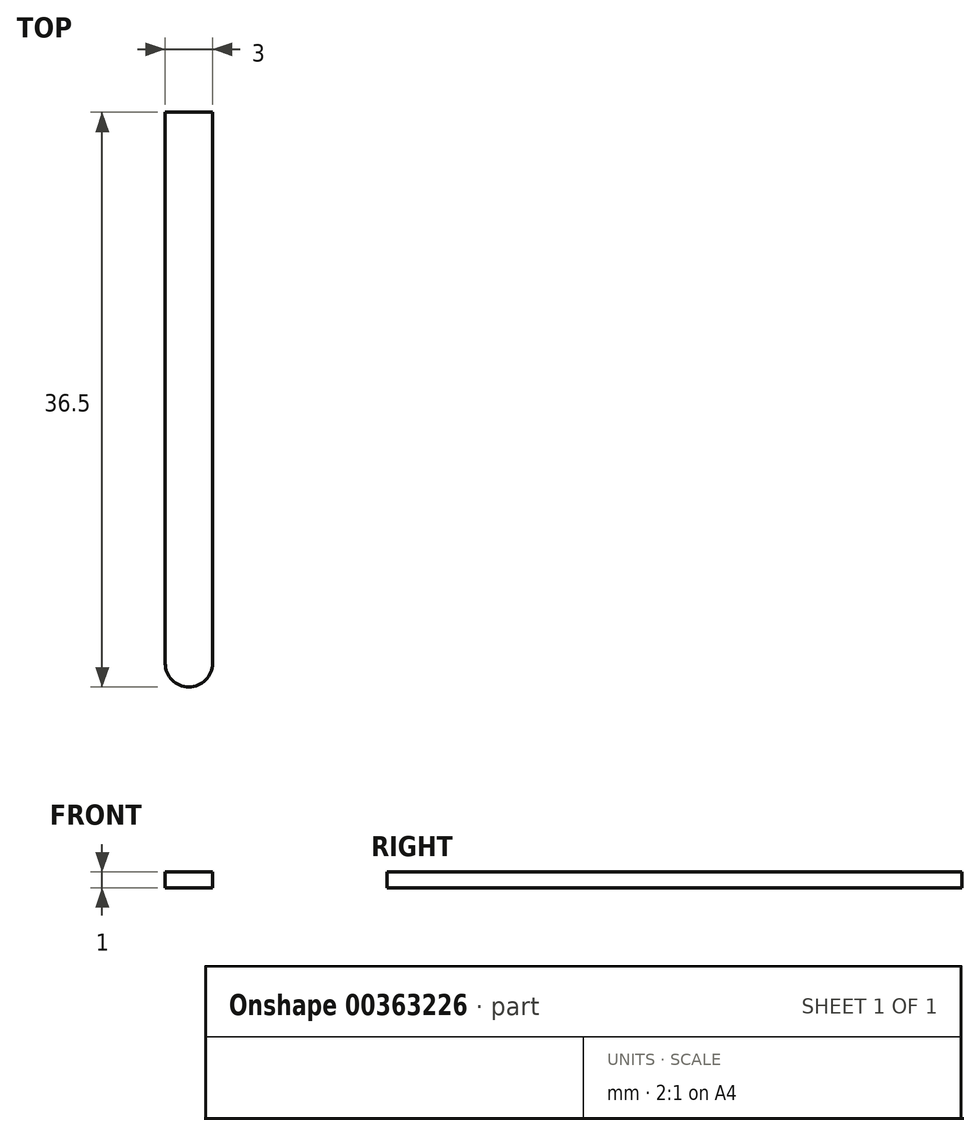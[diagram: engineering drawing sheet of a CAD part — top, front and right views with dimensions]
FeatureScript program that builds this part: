
annotation { "Feature Type Name" : "Feature", "Feature Type Description" : "" }
export const myFeature = defineFeature(function(context is Context, id is Id, definition is map)
    precondition{}
    {
        {
            var Q0;
            Q0=qCreatedBy(makeId("Top.planeOp"),FACE);
            var sketch = newSketch(context, id + "F0", { "sketchPlane" : qUnion([Q0])});
            skLineSegment(sketch, "E0.bottom", {"start": v(1.5, 17.5) * mm, "end": v(-1.5, 17.5) * mm});
            skLineSegment(sketch, "E0.top", {"start": v(1.5, -17.5) * mm, "end": v(-1.5, -17.5) * mm});
            skLineSegment(sketch, "E0.left", {"start": v(1.5, 17.5) * mm, "end": v(1.5, -17.5) * mm});
            skLineSegment(sketch, "E0.right", {"start": v(-1.5, 17.5) * mm, "end": v(-1.5, -17.5) * mm});
            skPoint(sketch, "E0.middle", {"position": v(0, 0) * mm});
            skArc(sketch, "E1", {"start": v(-1.5, -17.5) * mm, "mid": v(0, -19) * mm, "end": v(1.5, -17.5) * mm});
            skSolve(sketch);
        }
        {
            var Q0;
            Q0=makeQuery(id+"F0.imprint","IMPRINT",FACE,{"disambiguationData":[TD([[makeQuery(id+"F0.imprint","IMPRINT",EDGE,{"derivedFrom":sQuery(id+"F0.wireOp",EDGE,"E0.bottom")}),1.0]])]});
            var Q1;
            Q1=makeQuery(id+"F0.imprint","IMPRINT",FACE,{"disambiguationData":[TD([[makeQuery(id+"F0.imprint","IMPRINT",EDGE,{"derivedFrom":sQuery(id+"F0.wireOp",EDGE,"E0.top")}),1.0]])]});
            extrude(context, id + "F1", {"entities" : qUnion([Q0, Q1]), "depth" : 1 * mm});
        }
    });
